# Revit family: MSV-F2_DN15-150_PN25_RFA
name_source: partatom
category: Pipe Accessories
units: mm (PartAtom-declared; Revit-internal decimal feet)

## family parameters
Always vertical = Yes
Cut with Voids When Loaded = No
Part Type = Valve - Breaks Into
Round Connector Dimension = Use Diameter
Shared = No
Work Plane-Based = No

## types (11) — shared parameters
Connection = Flange
Description = Manual Balancing Valve
IfcExportAs = IfcValveType
IfcExportType = MSV-F2
LOD 200 = No
LOD 350 = Yes
Manufacturer = Danfoss
Max Flow Temperature = 150 °C
Max Pressure Drop = 2 bar
Nominal Pressure = 25 bar
URL = https://store.danfoss.com
Valve Body Material = Danfoss Ductile Iron

## per-type parameters (varying)
- MSV-F2_DN15_PN25_003Z1092: A1=40 mm; A2=19 mm; A3=10 mm; A4=13 mm; A5=10 mm; A6=39 mm; D=15 mm; D_V1=36 mm; H1=88 mm; H_A=34 mm; H_A1=0 mm  [stored 0 ft]; H_A1_ve=-30 mm  [stored -0.0984252 ft]; H_A2=4 mm  [stored 0.0131234 ft]; H_A2_ve=-4 mm; H_A3=10 mm; H_A4=5 mm  [stored 0.0164042 ft]; H_A5=8 mm; H_A6=12 mm; H_A7=7 mm  [stored 0.0229659 ft]; H_A8=33 mm; H_H1=-19 mm  [stored -0.062336 ft]; H_TP1=5 mm  [stored 0.0164042 ft]; H_TP2=-48 mm  [stored -0.15748 ft]; H_TP3=10 mm; H_TP4=10 mm; H_V1=15 mm; Kvs=3.1 m³/h; L1=2 mm  [stored 0.00656168 ft]; L1_ve=-2 mm  [stored -0.00656168 ft]; L2=12 mm; L2_ve=-12 mm  [stored -0.0393701 ft]; L3=11 mm; L3_1=12 mm; L4=8 mm; L5=8 mm; L6=8 mm; L_1=38 mm; L_2=92 mm; L_H1=78 mm; L_H2=14 mm; L_N1=1 mm  [stored 0.00328084 ft]; L_TP1=5 mm  [stored 0.0164042 ft]; Model=003Z1092; Model Type=MSV-F2_DN15_PN25; R_B1=18 mm; R_B2=19 mm; R_B3=14 mm; R_B4=15 mm; R_B5=18 mm; R_Flange1=25 mm; R_Flange2=48 mm; R_TP1=12 mm; R_TP2=10 mm; R_TP3=7 mm  [stored 0.0229659 ft]; R_TP4=1 mm  [stored 0.00328084 ft]; R_V1=18 mm; R_V2=13 mm; R_V2_2=13 mm; TD=95 mm; TH=136 mm; TL=130 mm; TP_Front=Yes; TP_Top=No; TP_Top Big=No; W_TP1=57 mm; W_TP2=48 mm; Weight=2.30 kg
- MSV-F2_DN20_PN25_003Z1093: A1=40 mm; A2=19 mm; A3=15 mm; A4=13 mm; A5=10 mm; A6=39 mm; D=20 mm; D_V1=33 mm; H1=90 mm; H_A=34 mm; H_A1=0 mm  [stored 0 ft]; H_A1_ve=-25 mm  [stored -0.082021 ft]; H_A2=9 mm; H_A2_ve=-9 mm  [stored -0.0295276 ft]; H_A3=10 mm; H_A4=5 mm  [stored 0.0164042 ft]; H_A5=7 mm  [stored 0.0229659 ft]; H_A6=12 mm; H_A7=7 mm  [stored 0.0229659 ft]; H_A8=35 mm; H_H1=-19 mm  [stored -0.062336 ft]; H_TP1=53 mm; H_TP2=9 mm; H_TP3=10 mm; H_TP4=5 mm  [stored 0.0164042 ft]; H_V1=15 mm; Kvs=6.3 m³/h; L1=2 mm  [stored 0.00656168 ft]; L1_ve=-2 mm  [stored -0.00656168 ft]; L2=14 mm; L2_ve=-14 mm  [stored -0.0459318 ft]; L3=13 mm; L3_1=12 mm; L4=8 mm; L5=8 mm; L6=12 mm; L_1=45 mm; L_2=105 mm; L_H1=78 mm; L_H2=14 mm; L_N1=5 mm  [stored 0.0164042 ft]; L_TP1=5 mm  [stored 0.0164042 ft]; Model=003Z1093; Model Type=MSV-F2_DN20_PN25; R_B1=19 mm; R_B2=19 mm; R_B3=15 mm; R_B4=15 mm; R_B5=18 mm; R_Flange1=30 mm; R_Flange2=53 mm; R_TP1=2 mm  [stored 0.00656168 ft]; R_TP2=10 mm; R_TP3=1 mm  [stored 0.00328084 ft]; R_TP4=1 mm  [stored 0.00328084 ft]; R_V1=17 mm; R_V2=15 mm; R_V2_2=15 mm; TD=105 mm; TH=143 mm; TL=150 mm; TP_Front=No; TP_Top=Yes; TP_Top Big=No; W_TP1=10 mm; W_TP2=10 mm; Weight=3.00 kg
- MSV-F2_DN25_PN25_003Z1094: A1=40 mm; A2=27 mm; A3=13 mm; A4=18 mm; A5=13 mm; A6=39 mm; D=25 mm; D_V1=41 mm; H1=100 mm; H_A=44 mm; H_A1=1 mm  [stored 0.00328084 ft]; H_A1_ve=-35 mm; H_A2=8 mm; H_A2_ve=-8 mm; H_A3=5 mm  [stored 0.0164042 ft]; H_A4=7 mm  [stored 0.0229659 ft]; H_A5=16 mm; H_A6=12 mm; H_A7=6 mm  [stored 0.019685 ft]; H_A8=33 mm; H_H1=-19 mm  [stored -0.062336 ft]; H_TP1=58 mm; H_TP2=9 mm; H_TP3=10 mm; H_TP4=10 mm; H_V1=22 mm; Kvs=9.0 m³/h; L1=3 mm  [stored 0.00984252 ft]; L1_ve=-3 mm; L2=13 mm; L2_ve=-13 mm; L3=13 mm; L3_1=19 mm; L4=5 mm  [stored 0.0164042 ft]; L5=13 mm; L6=25 mm; L_1=50 mm; L_2=110 mm; L_H1=78 mm; L_H2=14 mm; L_N1=6 mm  [stored 0.019685 ft]; L_TP1=5 mm  [stored 0.0164042 ft]; Model=003Z1094; Model Type=MSV-F2_DN25_PN25; R_B1=25 mm; R_B2=25 mm; R_B3=27 mm; R_B4=16 mm; R_B5=20 mm; R_Flange1=36 mm; R_Flange2=58 mm; R_TP1=2 mm  [stored 0.00656168 ft]; R_TP2=12 mm; R_TP3=2 mm  [stored 0.00656168 ft]; R_TP4=1 mm  [stored 0.00328084 ft]; R_V1=21 mm; R_V2=19 mm; R_V2_2=19 mm; TD=115 mm; TH=158 mm; TL=160 mm; TP_Front=No; TP_Top=Yes; TP_Top Big=No; W_TP1=10 mm; W_TP2=10 mm; Weight=3.80 kg
- MSV-F2_DN32_PN25_003Z1095: A1=40 mm; A2=26 mm; A3=11 mm; A4=15 mm; A5=11 mm; A6=39 mm; D=32 mm; D_V1=53 mm; H1=100 mm; H_A=48 mm; H_A1=0 mm  [stored 0 ft]; H_A1_ve=-15 mm  [stored -0.0492126 ft]; H_A2=33 mm; H_A2_ve=-33 mm; H_A3=9 mm; H_A4=6 mm  [stored 0.019685 ft]; H_A5=9 mm; H_A6=11 mm; H_A7=6 mm  [stored 0.019685 ft]; H_A8=32 mm; H_H1=-19 mm  [stored -0.062336 ft]; H_TP1=70 mm; H_TP2=9 mm; H_TP3=10 mm; H_TP4=10 mm; H_V1=20 mm; Kvs=15.5 m³/h; L1=3 mm  [stored 0.00984252 ft]; L1_ve=-3 mm; L2=17 mm; L2_ve=-17 mm; L3=12 mm; L3_1=18 mm; L4=5 mm  [stored 0.0164042 ft]; L5=8 mm; L6=27 mm; L_1=50 mm; L_2=130 mm; L_H1=78 mm; L_H2=14 mm; L_N1=6 mm  [stored 0.019685 ft]; L_TP1=5 mm  [stored 0.0164042 ft]; Model=003Z1095; Model Type=MSV-F2_DN32_PN25; R_B1=26 mm; R_B2=26 mm; R_B3=18 mm; R_B4=16 mm; R_B5=20 mm; R_Flange1=40 mm; R_Flange2=70 mm; R_TP1=2 mm  [stored 0.00656168 ft]; R_TP2=13 mm; R_TP3=15 mm; R_TP4=1 mm  [stored 0.00328084 ft]; R_V1=26 mm; R_V2=24 mm; R_V2_2=24 mm; TD=140 mm; TH=170 mm; TL=180 mm; TP_Front=No; TP_Top=Yes; TP_Top Big=No; W_TP1=10 mm; W_TP2=10 mm; Weight=5.80 kg
- MSV-F2_DN40_PN25_003Z1096: A1=45 mm; A2=32 mm; A3=11 mm; A4=15 mm; A5=11 mm; A6=39 mm; D=40 mm; D_V1=66 mm; H1=125 mm; H_A=59 mm; H_A1=0 mm  [stored 0 ft]; H_A1_ve=-54 mm; H_A2=5 mm  [stored 0.0164042 ft]; H_A2_ve=-5 mm  [stored -0.0164042 ft]; H_A3=17 mm; H_A4=6 mm  [stored 0.019685 ft]; H_A5=16 mm; H_A6=12 mm; H_A7=6 mm  [stored 0.019685 ft]; H_A8=33 mm; H_H1=-19 mm  [stored -0.062336 ft]; H_TP1=75 mm; H_TP2=9 mm; H_TP3=10 mm; H_TP4=10 mm; H_V1=25 mm; Kvs=32.3 m³/h; L1=3 mm  [stored 0.00984252 ft]; L1_ve=-3 mm; L2=17 mm; L2_ve=-17 mm; L3=18 mm; L3_1=21 mm; L4=6 mm  [stored 0.019685 ft]; L5=12 mm; L6=22 mm; L_1=63 mm; L_2=137 mm; L_H1=78 mm; L_H2=14 mm; L_N1=6 mm  [stored 0.019685 ft]; L_TP1=5 mm  [stored 0.0164042 ft]; Model=003Z1096; Model Type=MSV-F2_DN40_PN25; R_B1=31 mm; R_B2=32 mm; R_B3=17 mm; R_B4=15 mm; R_B5=19 mm; R_Flange1=45 mm; R_Flange2=75 mm; R_TP1=2 mm  [stored 0.00656168 ft]; R_TP2=14 mm; R_TP3=15 mm; R_TP4=9 mm; R_V1=33 mm; R_V2=28 mm; R_V2_2=28 mm; TD=150 mm; TH=200 mm; TL=200 mm; TP_Front=No; TP_Top=Yes; TP_Top Big=No; W_TP1=11 mm; W_TP2=10 mm; Weight=7.20 kg
- MSV-F2_DN50_PN25_003Z1070: A1=45 mm; A2=41 mm; A3=10 mm; A4=15 mm; A5=10 mm; A6=39 mm; D=50 mm; D_V1=77 mm; H1=125 mm; H_A=65 mm; H_A1=2 mm  [stored 0.00656168 ft]; H_A1_ve=-15 mm  [stored -0.0492126 ft]; H_A2=48 mm; H_A2_ve=-48 mm  [stored -0.15748 ft]; H_A3=8 mm; H_A4=15 mm; H_A5=27 mm; H_A6=10 mm; H_A7=7 mm  [stored 0.0229659 ft]; H_A8=32 mm; H_H1=-15 mm  [stored -0.0492126 ft]; H_TP1=10 mm; H_TP2=9 mm; H_TP3=92 mm; H_TP4=83 mm; H_V1=23 mm; Kvs=53.8 m³/h; L1=3 mm  [stored 0.00984252 ft]; L1_ve=-3 mm; L2=20 mm; L2_ve=-20 mm; L3=18 mm; L3_1=22 mm; L4=8 mm; L5=13 mm; L6=40 mm; L_1=67 mm; L_2=163 mm; L_H1=78 mm; L_H2=14 mm; L_N1=1 mm  [stored 0.00328084 ft]; L_TP1=5 mm  [stored 0.0164042 ft]; Model=003Z1070; Model Type=MSV-F2_DN50_PN25; R_B1=41 mm; R_B2=41 mm; R_B3=41 mm; R_B4=13 mm; R_B5=20 mm; R_Flange1=53 mm; R_Flange2=83 mm; R_TP1=2 mm  [stored 0.00656168 ft]; R_TP2=13 mm; R_TP3=15 mm; R_TP4=9 mm; R_V1=39 mm; R_V2=35 mm; R_V2_2=35 mm; TD=165 mm; TH=208 mm; TL=230 mm; TP_Front=No; TP_Top=Yes; TP_Top Big=Yes; W_TP1=11 mm; W_TP2=10 mm; Weight=9.40 kg
- MSV-F2_DN65_PN25_003Z1071: A1=80 mm; A2=60 mm; A3=23 mm; A4=40 mm; A5=23 mm; A6=70 mm; D=65 mm; D_V1=86 mm; H1=187 mm; H_A=77 mm; H_A1=10 mm; H_A1_ve=-35 mm; H_A2=32 mm; H_A2_ve=-32 mm; H_A3=25 mm; H_A4=19 mm; H_A5=42 mm; H_A6=12 mm; H_A7=10 mm; H_A8=46 mm; H_H1=-24 mm; H_TP1=93 mm; H_TP2=9 mm; H_TP3=84 mm; H_TP4=10 mm; H_V1=35 mm; Kvs=93.4 m³/h; L1=3 mm  [stored 0.00984252 ft]; L1_ve=-3 mm; L2=16 mm; L2_ve=-16 mm; L3=17 mm; L3_1=17 mm; L4=25 mm; L5=22 mm; L6=55 mm; L_1=97 mm; L_2=193 mm; L_H1=140 mm; L_H2=28 mm; L_N1=6 mm  [stored 0.019685 ft]; L_TP1=5 mm  [stored 0.0164042 ft]; Model=003Z1071; Model Type=MSV-F2_DN65_PN25; R_B1=55 mm; R_B2=46 mm; R_B3=60 mm; R_B4=28 mm; R_B5=33 mm; R_Flange1=62 mm; R_Flange2=93 mm; R_TP1=2 mm  [stored 0.00656168 ft]; R_TP2=12 mm; R_TP3=13 mm; R_TP4=9 mm; R_V1=43 mm; R_V2=39 mm; R_V2_2=39 mm; TD=185 mm; TH=280 mm; TL=290 mm; TP_Front=No; TP_Top=Yes; TP_Top Big=Yes; W_TP1=11 mm; W_TP2=10 mm; Weight=17.00 kg
- MSV-F2_DN80_PN25_003Z1072: A1=80 mm; A2=70 mm; A3=24 mm; A4=48 mm; A5=24 mm; A6=70 mm; D=80 mm; D_V1=106 mm; H1=207 mm; H_A=84 mm; H_A1=13 mm; H_A1_ve=-41 mm; H_A2=30 mm; H_A2_ve=-30 mm  [stored -0.0984252 ft]; H_A3=25 mm; H_A4=24 mm; H_A5=56 mm; H_A6=14 mm; H_A7=12 mm; H_A8=48 mm; H_H1=-22 mm; H_TP1=40 mm; H_TP2=9 mm; H_TP3=109 mm; H_TP4=100 mm; H_V1=65 mm; Kvs=122.3 m³/h; L1=3 mm  [stored 0.00984252 ft]; L1_ve=-3 mm; L2=16 mm; L2_ve=-16 mm; L3=20 mm; L3_1=20 mm; L4=21 mm; L5=35 mm; L6=48 mm; L_1=106 mm; L_2=204 mm; L_H1=140 mm; L_H2=28 mm; L_N1=1 mm  [stored 0.00328084 ft]; L_TP1=1 mm  [stored 0.00328084 ft]; Model=003Z1072; Model Type=MSV-F2_DN80_PN25; R_B1=70 mm; R_B2=58 mm; R_B3=70 mm; R_B4=27 mm; R_B5=33 mm; R_Flange1=69 mm; R_Flange2=100 mm; R_TP1=2 mm  [stored 0.00656168 ft]; R_TP2=10 mm; R_TP3=15 mm; R_TP4=7 mm  [stored 0.0229659 ft]; R_V1=53 mm; R_V2=48 mm; R_V2_2=48 mm; TD=200 mm; TH=307 mm; TL=310 mm; TP_Front=No; TP_Top=No; TP_Top Big=Yes; W_TP1=11 mm; W_TP2=10 mm; Weight=21.00 kg
- MSV-F2_DN100_PN25_003Z1073: A1=75 mm; A2=90 mm; A3=26 mm; A4=60 mm; A5=26 mm; A6=70 mm; D=100 mm; D_V1=132 mm; H1=223 mm; H_A=107 mm; H_A1=13 mm; H_A1_ve=-50 mm  [stored -0.164042 ft]; H_A2=42 mm; H_A2_ve=-42 mm; H_A3=26 mm; H_A4=26 mm; H_A5=53 mm; H_A6=13 mm; H_A7=9 mm; H_A8=49 mm; H_H1=-27 mm; H_TP1=40 mm; H_TP2=9 mm; H_TP3=119 mm; H_TP4=110 mm; H_V1=70 mm; Kvs=200.0 m³/h; L1=3 mm  [stored 0.00984252 ft]; L1_ve=-3 mm; L2=16 mm; L2_ve=-16 mm; L3=16 mm; L3_1=25 mm; L4=18 mm; L5=42 mm; L6=80 mm; L_1=120 mm; L_2=230 mm; L_H1=140 mm; L_H2=28 mm; L_N1=1 mm  [stored 0.00328084 ft]; L_TP1=1 mm  [stored 0.00328084 ft]; Model=003Z1073; Model Type=MSV-F2_DN100_PN25; R_B1=85 mm; R_B2=70 mm; R_B3=90 mm; R_B4=27 mm; R_B5=33 mm; R_Flange1=81 mm; R_Flange2=110 mm; R_TP1=1 mm  [stored 0.00328084 ft]; R_TP2=11 mm; R_TP3=15 mm; R_TP4=9 mm; R_V1=66 mm; R_V2=60 mm; R_V2_2=60 mm; TD=220 mm; TH=333 mm; TL=350 mm; TP_Front=No; TP_Top=No; TP_Top Big=Yes; W_TP1=11 mm; W_TP2=10 mm; Weight=33.00 kg
- MSV-F2_DN125_PN25_003Z1074: A1=80 mm; A2=98 mm; A3=25 mm; A4=75 mm; A5=25 mm; A6=70 mm; D=125 mm; D_V1=165 mm; H1=252 mm; H_A=108 mm; H_A1=10 mm; H_A1_ve=-63 mm; H_A2=35 mm; H_A2_ve=-35 mm; H_A3=52 mm; H_A4=30 mm; H_A5=57 mm; H_A6=13 mm; H_A7=9 mm; H_A8=45 mm; H_H1=-23 mm; H_TP1=40 mm; H_TP2=-1 mm  [stored -0.00328084 ft]; H_TP3=134 mm; H_TP4=125 mm; H_V1=60 mm; Kvs=304.4 m³/h; L1=3 mm  [stored 0.00984252 ft]; L1_ve=-3 mm; L2=16 mm; L2_ve=-16 mm; L3=25 mm; L3_1=21 mm; L4=38 mm; L5=31 mm; L6=82 mm; L_1=144 mm; L_2=256 mm; L_H1=140 mm; L_H2=28 mm; L_N1=1 mm  [stored 0.00328084 ft]; L_TP1=1 mm  [stored 0.00328084 ft]; Model=003Z1074; Model Type=MSV-F2_DN125_PN25; R_B1=95 mm; R_B2=84 mm; R_B3=98 mm; R_B4=28 mm; R_B5=33 mm; R_Flange1=95 mm; R_Flange2=125 mm; R_TP1=2 mm  [stored 0.00656168 ft]; R_TP2=13 mm; R_TP3=15 mm; R_TP4=7 mm  [stored 0.0229659 ft]; R_V1=83 mm; R_V2=75 mm; R_V2_2=75 mm; TD=250 mm; TH=377 mm; TL=400 mm; TP_Front=No; TP_Top=No; TP_Top Big=Yes; W_TP1=11 mm; W_TP2=10 mm; Weight=44.00 kg
- MSV-F2_DN150_PN25_003Z1075: A1=80 mm; A2=112 mm; A3=25 mm; A4=77 mm; A5=25 mm; A6=70 mm; D=150 mm; D_V1=198 mm; H1=248 mm; H_A=133 mm; H_A1=22 mm; H_A1_ve=-55 mm; H_A2=56 mm; H_A2_ve=-56 mm; H_A3=46 mm; H_A4=12 mm; H_A5=35 mm; H_A6=13 mm; H_A7=8 mm; H_A8=45 mm; H_H1=-24 mm; H_TP1=40 mm; H_TP2=9 mm; H_TP3=151 mm; H_TP4=143 mm; H_V1=50 mm; Kvs=400.8 m³/h; L1=3 mm  [stored 0.00984252 ft]; L1_ve=-3 mm; L2=17 mm; L2_ve=-17 mm; L3=7 mm  [stored 0.0229659 ft]; L3_1=21 mm; L4=50 mm; L5=60 mm; L6=80 mm; L_1=176 mm; L_2=304 mm; L_H1=140 mm; L_H2=28 mm; L_N1=1 mm  [stored 0.00328084 ft]; L_TP1=2 mm  [stored 0.00656168 ft]; Model=003Z1075; Model Type=MSV-F2_DN150_PN25; R_B1=112 mm; R_B2=95 mm; R_B3=110 mm; R_B4=26 mm; R_B5=32 mm; R_Flange1=109 mm; R_Flange2=143 mm; R_TP1=2 mm  [stored 0.00656168 ft]; R_TP2=13 mm; R_TP3=15 mm; R_TP4=9 mm; R_V1=99 mm; R_V2=90 mm; R_V2_2=90 mm; TD=285 mm; TH=391 mm; TL=480 mm; TP_Front=No; TP_Top=No; TP_Top Big=Yes; W_TP1=11 mm; W_TP2=10 mm; Weight=56.50 kg

note: [stored X ft] marks values corroborated as IEEE doubles in the binary element streams (Revit-internal decimal feet)

## geometry (parser evidence)
native form markers: Sweep x6
no freeform markers — native parametric forms only
